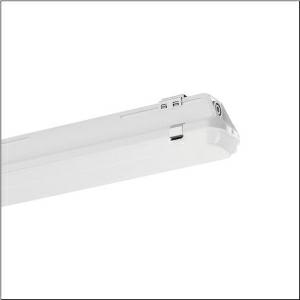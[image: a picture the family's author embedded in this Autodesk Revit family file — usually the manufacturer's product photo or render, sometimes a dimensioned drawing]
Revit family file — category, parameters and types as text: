
# Revit family: monsun_r__21_51fb107p460b_c23d
name_source: partatom
category: Lighting Fixtures
units: mm (PartAtom-declared; Revit-internal decimal feet)

## family parameters
Cut with Voids When Loaded = No
Host = Face
Light Source = No
Part Type = Normal
Room Calculation Point = No
Round Connector Dimension = Use Diameter
Shared = No

## types (1)
- Monsun® 21 (1 x LED, 6000 lm, 38 W, 4000K)
    Apparent Load = 38 VA
    CIE Flux Codes = 47 77 93 94 100
    Color Rendering = 80
    Color Temperature = 4000K
    Default Elevation = 1800 mm
    Description = Monsun® 21, damp-proof luminaire, chain hanger, primary optical cover: enclosure, of PMMA, light emission: direct distribution, primary light characteristic: symmetric, installation type: suspended mounting, surface-mounted, horizontal mounting, vertical mounting, LED, rated luminous flux: 6.000lm, luminous efficacy: 158lm/W, light colour: 840, colour temperature: 4000K, control gear: ECG, with terminal, 3-pole, max. 2.5mm², mains connection: 220..240V, AC, 50/60Hz, rated input power: 38W, housing, of glass-fibre reinforced polyester, uncoated, bright grey, length: 1.590mm, width: 90mm, height: 88mm, clip for enclosure, of stainless steel (V2A), ceiling mounting element, of stainless steel (V2A), chain hanger, of stainless steel (V2A), protection rating (complete): IP66, insulation class (complete): insulation class I (protective earthing), certification: CE, ENEC, VDE, UKCA, protection symbol: D, impact resistance: IK04, permissible operating ambient temperature: -25..+35°C, standard: EN 50419, EN 60598-2-1, corresponds to IFS (International Featured Standards) requirements for safety and quality in the food industry, for indoor or canopied outdoor use, no direct snow, no direct sun, no direct rain, packaging unit: 1 piece
    Height = 89 mm
    Lamp = 1 x LED
    Lamp Light Flux = 6000 lm
    Lamp Power = 38 W
    Lamp count = 1
    Length = 1590 mm
    Luminous efficacy = 158 lm/W
    Manufacturer = Siteco
    ModVariant = No
    Model = 51FB107P460B
    Mounting Place = Ceiling
    Mounting Type = Pendant
    Number of Poles = 1
    OnlyDefault = Yes
    Power Factor = 1
    Product Name = Monsun® 21
    Product group = damp-proof luminaire | ceiling pendant
    ProductGroupID = 908
    Protection Class = Protection class I
    Protection Degree = IP 66
    RLX_Detail_Level = 1
    RlxData = <blob elided: 88209 chars, md5=c8f993b7>
    Socket = socket
    Standby Power = 0 W
    System Light Flux = 6000 lm
    System Power = 38 W
    Type Comments = Product without accessories
    Type Image = l_1006717.jpg
    URL = http://relux.com
    VarID = ---
    Voltage = 0 V
    Weight = 0.00 kg
    Width = 90 mm

## geometry (parser evidence)
native form markers: Blend x4, Sweep x11
no freeform markers — native parametric forms only
